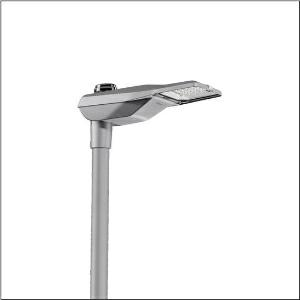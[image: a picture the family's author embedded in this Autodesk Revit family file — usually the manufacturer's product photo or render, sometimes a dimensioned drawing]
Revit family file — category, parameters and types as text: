
# Revit family: streetlight_sl_21_micro___st1_0a_5xe5d67n08db_977e
name_source: partatom
category: Lighting Fixtures
units: mm (PartAtom-declared; Revit-internal decimal feet)

## family parameters
Cut with Voids When Loaded = No
Host = Face
Light Source = No
Part Type = Normal
Room Calculation Point = No
Round Connector Dimension = Use Diameter
Shared = No

## types (1)
- --- (1 x LED, 4580 lm, 39.1 W, 2700K)
    Apparent Load = 39 VA
    CIE Flux Codes = 37 72 97 100 100
    Color Rendering = 70
    Color Temperature = 2700K
    Default Elevation = 1800 mm
    Description = Streetlight SL 21 micro, mast luminaire, primary light control with lens, of PMMA, primary optical cover: cover, of toughened safety glass, transparent, light distribution: ST1.0a, light emission: direct distribution, primary light characteristic: asymmetric, installation type: post-top, LED, 3G 1.5mm², High Power LED, rated luminous flux: 4.580lm, luminous efficacy: 117lm/W, light colour: 727, colour temperature: 2700K, control: overheat protection, presetting dimming linear, constant luminous flux control, time-dependent luminous flux control, flexible luminous flux parameterisation, mains connection: 230..240V, AC, 50/60Hz, connection cable pre-assembled, cable length: 6,5m, wiring characteristics: H07RN-F, start of lifetime: 39W, end of service life: 41W, reduction: 18W, luminaire housing, of diecast aluminium (EN AC-44300), powder-coated, Siteco® metallic grey (DB 702S), corrosivity category C5 mid according to DIN EN ISO 12944, multi-level sealing system, sealing non-destructively replaceable, inclination adjustable: 0°, 5°, 10°, 15°, length: 528mm, width: 235mm, height: 110mm, spigot size: 76/60mm (post-top), protection rating (complete): IP66, insulation class (complete): insulation class I (protective earthing), certification: CE, ENEC, ENEC+, VDE, impact resistance: IK09, permissible operating ambient temperature for outdoor applications: -40..+50°C, standard-compliant lighting for roads and squares, packaging unit: 1 piece

Light Distribution: ST1.0a
    Height = 110 mm
    Lamp = 1 x LED
    Lamp Light Flux = 4580 lm
    Lamp Power = 39.1 W
    Lamp count = 1
    Length = 528 mm
    Luminous efficacy = 117 lm/W
    Manufacturer = Siteco
    ModVariant = No
    Model = 5XE5D67N08DB
    Number of Poles = 1
    OnlyDefault = Yes
    Power Factor = 1
    Product Name = Streetlight SL 21 micro | ST1.0a
    Product group = mast luminaire | pylon top
    ProductGroupID = 6100
    Protection Class = Protection class I
    Protection Degree = IP 66
    RLX_Detail_Level = 1
    RLX_Emergency_Light_Flux = 0 lm
    RLX_Emergency_Type = 0
    RLX_Emergency_Type_DB = No
    RlxData = <blob elided: 98701 chars, md5=2c525e68>
    Socket = socket
    Standby Power = 0 W
    System Light Flux = 4580 lm
    System Power = 39 W
    Type Comments = factory setting: luminous flux: 100 % | dim-lin: 254 | 765 mA
    Type Image = l_1294375.jpg
    URL = http://relux.com
    VarID = @adj_085777
    Voltage = 0 V
    Weight = 0.00 kg
    Width = 235 mm

## geometry (parser evidence)
native form markers: Blend x4, Sweep x9
no freeform markers — native parametric forms only
